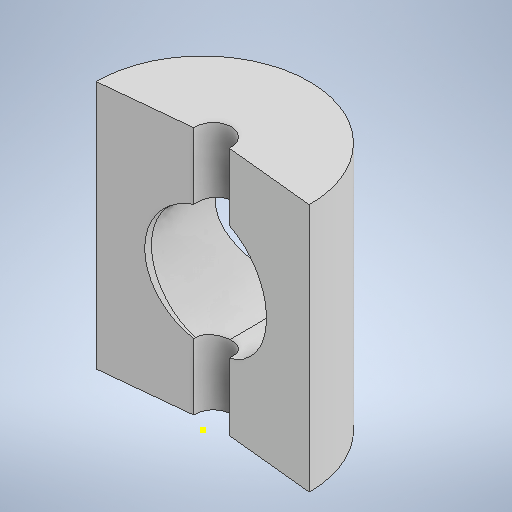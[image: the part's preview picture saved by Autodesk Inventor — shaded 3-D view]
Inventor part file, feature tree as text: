
AUTODESK INVENTOR PART (.ipt)
format: ipt  version: 2025.2 (Build 292293000, 293)  size: 251,904 bytes
history: native  units: in
note: dims shown in document units (in); Inventor stores cm internally (conversion verified against a paired STEP export)
features: sketch x6, extrude x4
ambient origin geometry x8: Origin, YZ Plane, XZ Plane, XY Plane, X Axis, Y Axis, Z Axis, Center Point
bodies: Solid1 (feature_tree)
feature tree (10):
  sketch  "Sketch1"  dims[d0=0.0591in d1=1.1811in]
  extrude  "Extrusion1"  Depth=0.0591in
  extrude  "Extrusion2"  Depth=1.378in TaperAngle=0.0deg
  extrude  "Extrusion3"  Depth=1.378in TaperAngle=0.0deg
  extrude  "Extrusion4"  Depth=1.378in TaperAngle=0.0deg
  sketch  "Sketch6"
  sketch  "Sketch2"  dims[d2=0.1969in d3=1.378in d4=0.0in]
  sketch  "Sketch3"  dims[d5=0.6693in d6=1.378in d7=0.0in]
  sketch  "Sketch4"  dims[d8=1.378in d9=0.0in d10=1.378in d11=0.0in]
  sketch  "Sketch5"
